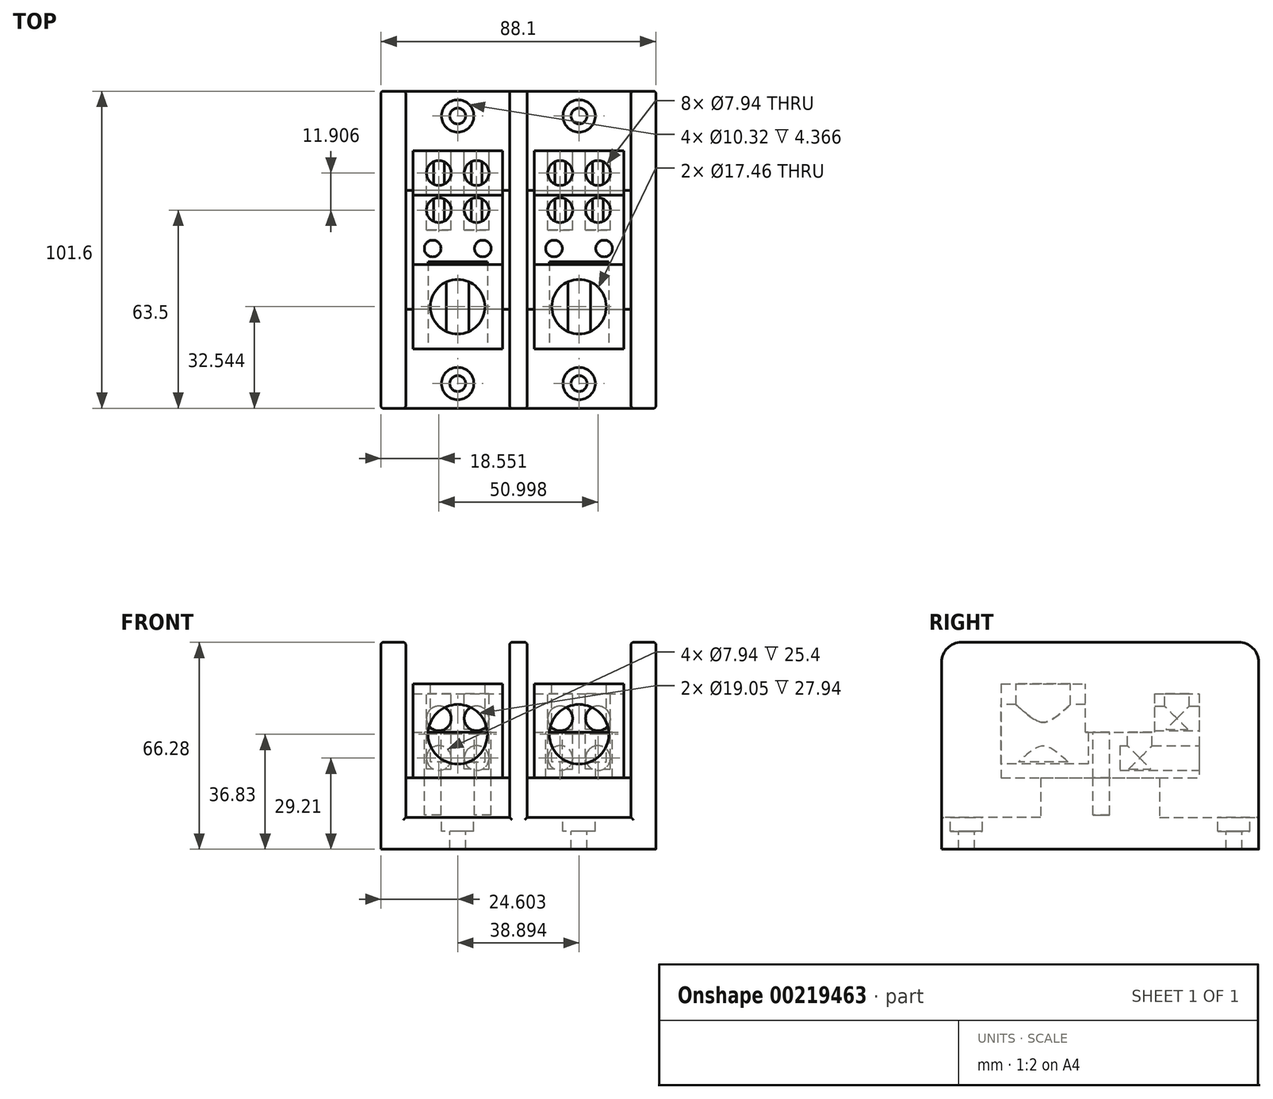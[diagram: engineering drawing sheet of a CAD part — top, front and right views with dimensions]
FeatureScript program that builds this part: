
annotation { "Feature Type Name" : "Feature", "Feature Type Description" : "" }
export const myFeature = defineFeature(function(context is Context, id is Id, definition is map)
    precondition{}
    {
        {
            var Q0;
            Q0=qCreatedBy(makeId("Top.planeOp"),FACE);
            var sketch = newSketch(context, id + "F0", { "sketchPlane" : qUnion([Q0])});
            skLineSegment(sketch, "E0.bottom", {"start": v(-44.05, -50.8) * mm, "end": v(44.05, -50.8) * mm});
            skLineSegment(sketch, "E0.top", {"start": v(-44.05, 50.8) * mm, "end": v(44.05, 50.8) * mm});
            skLineSegment(sketch, "E0.left", {"start": v(-44.05, -50.8) * mm, "end": v(-44.05, 50.8) * mm});
            skLineSegment(sketch, "E0.right", {"start": v(44.05, -50.8) * mm, "end": v(44.05, 50.8) * mm});
            skPoint(sketch, "E0.middle", {"position": v(0, 0) * mm});
            skSolve(sketch);
        }
        {
            var Q0;
            Q0=makeQuery(id+"F0.imprint","IMPRINT",FACE,{"disambiguationData":[TD([[makeQuery(id+"F0.imprint","IMPRINT",EDGE,{"derivedFrom":sQuery(id+"F0.wireOp",EDGE,"E0.bottom")}),1.0]])]});
            extrude(context, id + "F1", {"entities" : qUnion([Q0]), "depth" : 10.16 * mm});
        }
        {
            var Q0;
            Q0=makeQuery(id+"F1.opExtrude","CAP_FACE",FACE,{"disambiguationData":[OSD([sQuery(id+"F0.wireOp",EDGE,"E0.bottom"),sQuery(id+"F0.wireOp",EDGE,"E0.top"),sQuery(id+"F0.wireOp",EDGE,"E0.left"),sQuery(id+"F0.wireOp",EDGE,"E0.right")])],"isStart":false});
            var sketch = newSketch(context, id + "F2", { "sketchPlane" : qUnion([Q0])});
            skCircle(sketch, "E1", {"center": v(-19.45, 42.86) * mm, "radius": 2.54 * mm});
            skCircle(sketch, "E2", {"center": v(19.45, 42.86) * mm, "radius": 2.54 * mm});
            skCircle(sketch, "E3", {"center": v(-19.45, -42.86) * mm, "radius": 2.54 * mm});
            skCircle(sketch, "E4", {"center": v(19.45, -42.86) * mm, "radius": 2.54 * mm});
            skSolve(sketch);
        }
        {
            var Q0;
            Q0=qSketchRegion(id+"F2",true);
            extrude(context, id + "F3", {"entities" : qUnion([Q0]), "operationType" : NewBodyOperationType.REMOVE, "oppositeDirection" : true, "depth" : 10.16 * mm});
        }
        {
            var Q0;
            Q0=makeQuery(id+"F1.opExtrude","CAP_FACE",FACE,{"disambiguationData":[OSD([sQuery(id+"F0.wireOp",EDGE,"E0.bottom"),sQuery(id+"F0.wireOp",EDGE,"E0.top"),sQuery(id+"F0.wireOp",EDGE,"E0.left"),sQuery(id+"F0.wireOp",EDGE,"E0.right")])],"isStart":false});
            var sketch = newSketch(context, id + "F4", { "sketchPlane" : qUnion([Q0])});
            skCircle(sketch, "E5", {"center": v(-19.45, 42.86) * mm, "radius": 5.16 * mm});
            skCircle(sketch, "E6", {"center": v(19.45, 42.86) * mm, "radius": 5.16 * mm});
            skCircle(sketch, "E7", {"center": v(-19.45, -42.86) * mm, "radius": 5.16 * mm});
            skCircle(sketch, "E8", {"center": v(19.45, -42.86) * mm, "radius": 5.16 * mm});
            skSolve(sketch);
        }
        {
            var Q0;
            Q0=qSketchRegion(id+"F4",true);
            extrude(context, id + "F5", {"entities" : qUnion([Q0]), "operationType" : NewBodyOperationType.REMOVE, "oppositeDirection" : true, "depth" : 4.37 * mm});
        }
        {
            var Q0;
            Q0=makeQuery(id+"F1.opExtrude","CAP_FACE",FACE,{"disambiguationData":[OSD([sQuery(id+"F0.wireOp",EDGE,"E0.bottom"),sQuery(id+"F0.wireOp",EDGE,"E0.top"),sQuery(id+"F0.wireOp",EDGE,"E0.left"),sQuery(id+"F0.wireOp",EDGE,"E0.right")])],"isStart":false});
            var sketch = newSketch(context, id + "F6", { "sketchPlane" : qUnion([Q0])});
            skLineSegment(sketch, "E9.bottom", {"start": v(-2.78, -19.05) * mm, "end": v(-36.12, -19.05) * mm});
            skLineSegment(sketch, "E9.top", {"start": v(-2.78, 19.05) * mm, "end": v(-36.12, 19.05) * mm});
            skLineSegment(sketch, "E9.left", {"start": v(-2.78, -19.05) * mm, "end": v(-2.78, 19.05) * mm});
            skLineSegment(sketch, "E9.right", {"start": v(-36.12, -19.05) * mm, "end": v(-36.12, 19.05) * mm});
            skPoint(sketch, "E9.middle", {"position": v(-19.45, 0) * mm});
            skLineSegment(sketch, "E10.bottom", {"start": v(2.78, -19.05) * mm, "end": v(36.12, -19.05) * mm});
            skLineSegment(sketch, "E10.top", {"start": v(2.78, 19.05) * mm, "end": v(36.12, 19.05) * mm});
            skLineSegment(sketch, "E10.left", {"start": v(2.78, -19.05) * mm, "end": v(2.78, 19.05) * mm});
            skLineSegment(sketch, "E10.right", {"start": v(36.12, -19.05) * mm, "end": v(36.12, 19.05) * mm});
            skPoint(sketch, "E10.middle", {"position": v(19.45, 0) * mm});
            skSolve(sketch);
        }
        {
            var Q0;
            Q0=qSketchRegion(id+"F6",true);
            extrude(context, id + "F7", {"entities" : qUnion([Q0]), "operationType" : NewBodyOperationType.ADD, "depth" : 12.7 * mm});
        }
        {
            var Q0;
            Q0=makeQuery(id+"F1.opExtrude","CAP_FACE",FACE,{"disambiguationData":[OSD([sQuery(id+"F0.wireOp",EDGE,"E0.bottom"),sQuery(id+"F0.wireOp",EDGE,"E0.top"),sQuery(id+"F0.wireOp",EDGE,"E0.left"),sQuery(id+"F0.wireOp",EDGE,"E0.right")])],"isStart":false});
            var sketch = newSketch(context, id + "F8", { "sketchPlane" : qUnion([Q0])});
            skLineSegment(sketch, "E11.bottom", {"start": v(-36.12, 50.8) * mm, "end": v(-44.05, 50.8) * mm});
            skLineSegment(sketch, "E11.top", {"start": v(-36.12, -50.8) * mm, "end": v(-44.05, -50.8) * mm});
            skLineSegment(sketch, "E11.left", {"start": v(-36.12, 50.8) * mm, "end": v(-36.12, -50.8) * mm});
            skLineSegment(sketch, "E11.right", {"start": v(-44.05, 50.8) * mm, "end": v(-44.05, -50.8) * mm});
            skLineSegment(sketch, "E12.bottom", {"start": v(2.78, 50.8) * mm, "end": v(-2.78, 50.8) * mm});
            skLineSegment(sketch, "E12.top", {"start": v(2.78, -50.8) * mm, "end": v(-2.78, -50.8) * mm});
            skLineSegment(sketch, "E12.left", {"start": v(2.78, 50.8) * mm, "end": v(2.78, -50.8) * mm});
            skLineSegment(sketch, "E12.right", {"start": v(-2.78, 50.8) * mm, "end": v(-2.78, -50.8) * mm});
            skLineSegment(sketch, "E13.bottom", {"start": v(36.12, 50.8) * mm, "end": v(44.05, 50.8) * mm});
            skLineSegment(sketch, "E13.top", {"start": v(36.12, -50.8) * mm, "end": v(44.05, -50.8) * mm});
            skLineSegment(sketch, "E13.left", {"start": v(36.12, 50.8) * mm, "end": v(36.12, -50.8) * mm});
            skLineSegment(sketch, "E13.right", {"start": v(44.05, 50.8) * mm, "end": v(44.05, -50.8) * mm});
            skSolve(sketch);
        }
        {
            var Q0;
            Q0=qSketchRegion(id+"F8",true);
            extrude(context, id + "F9", {"entities" : qUnion([Q0]), "operationType" : NewBodyOperationType.ADD, "depth" : 56.12 * mm});
        }
        {
            var Q0;
            Q0=makeQuery(id+"F7.opExtrude","CAP_FACE",FACE,{"disambiguationData":[OSD([sQuery(id+"F6.wireOp",EDGE,"E9.bottom"),sQuery(id+"F6.wireOp",EDGE,"E9.top"),sQuery(id+"F6.wireOp",EDGE,"E9.left"),sQuery(id+"F6.wireOp",EDGE,"E9.right")])],"isStart":false});
            var sketch = newSketch(context, id + "F10", { "sketchPlane" : qUnion([Q0])});
            skLineSegment(sketch, "E14.bottom", {"start": v(-33.83, -31.75) * mm, "end": v(-5.06, -31.75) * mm});
            skLineSegment(sketch, "E14.top", {"start": v(-33.83, 31.75) * mm, "end": v(-5.06, 31.75) * mm});
            skLineSegment(sketch, "E14.left", {"start": v(-33.83, -31.75) * mm, "end": v(-33.83, 31.75) * mm});
            skLineSegment(sketch, "E14.right", {"start": v(-5.06, -31.75) * mm, "end": v(-5.06, 31.75) * mm});
            skPoint(sketch, "E14.middle", {"position": v(-19.45, 0) * mm});
            skSolve(sketch);
        }
        {
            var Q0;
            Q0=qSketchRegion(id+"F10",true);
            extrude(context, id + "F11", {"entities" : qUnion([Q0]), "depth" : 30.16 * mm});
        }
        {
            var Q0;
            Q0=makeQuery(id+"F11.opExtrude","CAP_FACE",FACE,{"disambiguationData":[OSD([sQuery(id+"F10.wireOp",EDGE,"E14.bottom"),sQuery(id+"F10.wireOp",EDGE,"E14.top"),sQuery(id+"F10.wireOp",EDGE,"E14.left"),sQuery(id+"F10.wireOp",EDGE,"E14.right")])],"isStart":false});
            var sketch = newSketch(context, id + "F12", { "sketchPlane" : qUnion([Q0])});
            skLineSegment(sketch, "E15.bottom", {"start": v(-33.83, -4.76) * mm, "end": v(-5.06, -4.76) * mm});
            skLineSegment(sketch, "E15.top", {"start": v(-33.83, 17.46) * mm, "end": v(-5.06, 17.46) * mm});
            skLineSegment(sketch, "E15.left", {"start": v(-33.83, -4.76) * mm, "end": v(-33.83, 17.46) * mm});
            skLineSegment(sketch, "E15.right", {"start": v(-5.06, -4.76) * mm, "end": v(-5.06, 17.46) * mm});
            skPoint(sketch, "E15.middle", {"position": v(-19.45, 6.35) * mm});
            skPoint(sketch, "E15.middle.positionSnap0", {"position": v(-19.45, -31.75) * mm});
            skPoint(sketch, "E15.centerSnap0", {"position": v(-19.45, -31.75) * mm});
            skSolve(sketch);
        }
        {
            var Q0;
            Q0=makeQuery(id+"F12.imprint","IMPRINT",FACE,{"disambiguationData":[TD([[makeQuery(id+"F12.imprint","IMPRINT",EDGE,{"derivedFrom":sQuery(id+"F12.wireOp",EDGE,"E15.bottom")}),1.0]])]});
            extrude(context, id + "F13", {"entities" : qUnion([Q0]), "operationType" : NewBodyOperationType.REMOVE, "oppositeDirection" : true, "depth" : 15.48 * mm});
        }
        {
            var Q0;
            {var subQ0=sQuery(id+"F10.wireOp",EDGE,"E14.top");var subQ1=sQuery(id+"F10.wireOp",EDGE,"E14.right");var subQ2=sQuery(id+"F10.wireOp",EDGE,"E14.left");Q0=makeQuery(id+"F13.boolean.opBoolean","SPLIT",FACE,{"disambiguationData":[TD([makeQuery(id+"F11.opExtrude","SWEPT_FACE",FACE,{"disambiguationData":[OSD([subQ0])]})])],"derivedFrom":makeQuery(id+"F11.opExtrude","CAP_FACE",FACE,{"disambiguationData":[OSD([sQuery(id+"F10.wireOp",EDGE,"E14.bottom"),subQ0,subQ2,subQ1])],"isStart":false})});}
            extrude(context, id + "F14", {"entities" : qUnion([Q0]), "operationType" : NewBodyOperationType.REMOVE, "oppositeDirection" : true, "depth" : 3.17 * mm});
        }
        {
            var Q0;
            {var subQ0=sQuery(id+"F10.wireOp",EDGE,"E14.bottom");var subQ1=sQuery(id+"F10.wireOp",EDGE,"E14.left");var subQ2=sQuery(id+"F10.wireOp",EDGE,"E14.right");Q0=makeQuery(id+"F13.boolean.opBoolean","SPLIT",FACE,{"disambiguationData":[TD([makeQuery(id+"F11.opExtrude","SWEPT_FACE",FACE,{"disambiguationData":[OSD([subQ0])]})])],"derivedFrom":makeQuery(id+"F11.opExtrude","CAP_FACE",FACE,{"disambiguationData":[OSD([subQ0,sQuery(id+"F10.wireOp",EDGE,"E14.top"),subQ1,subQ2])],"isStart":false})});}
            var sketch = newSketch(context, id + "F15", { "sketchPlane" : qUnion([Q0])});
            skCircle(sketch, "E16", {"center": v(-19.45, -18.26) * mm, "radius": 8.73 * mm});
            skPoint(sketch, "E16.centerSnap0", {"position": v(-5.06, -18.26) * mm});
            skPoint(sketch, "E16.centerSnap1", {"position": v(-19.45, -4.76) * mm});
            skSolve(sketch);
        }
        {
            var Q0;
            Q0=makeQuery(id+"F15.imprint","IMPRINT",FACE,{"disambiguationData":[TD([[makeQuery(id+"F15.imprint","IMPRINT",EDGE,{"derivedFrom":sQuery(id+"F15.wireOp",EDGE,"E16")}),1.0]])]});
            extrude(context, id + "F16", {"entities" : qUnion([Q0]), "operationType" : NewBodyOperationType.REMOVE, "oppositeDirection" : true, "depth" : 25 * mm});
        }
        {
            var Q0;
            Q0=makeQuery(id+"F11.opExtrude","SWEPT_FACE",FACE,{"disambiguationData":[OSD([sQuery(id+"F10.wireOp",EDGE,"E14.bottom")])]});
            var sketch = newSketch(context, id + "F17", { "sketchPlane" : qUnion([Q0])});
            skCircle(sketch, "E17", {"center": v(-19.45, 36.83) * mm, "radius": 9.53 * mm});
            skPoint(sketch, "E17.centerSnap0", {"position": v(-19.45, 53.02) * mm});
            skSolve(sketch);
        }
        {
            var Q0;
            Q0=makeQuery(id+"F17.imprint","IMPRINT",FACE,{"disambiguationData":[TD([[makeQuery(id+"F17.imprint","IMPRINT",EDGE,{"derivedFrom":sQuery(id+"F17.wireOp",EDGE,"E17")}),1.0]])]});
            extrude(context, id + "F18", {"entities" : qUnion([Q0]), "operationType" : NewBodyOperationType.REMOVE, "oppositeDirection" : true, "depth" : 27.94 * mm});
        }
        {
            var Q0;
            Q0=makeQuery(id+"F13.boolean.opBoolean","COPY",FACE,{"derivedFrom":makeQuery(id+"F13.opExtrude","CAP_FACE",FACE,{"disambiguationData":[OSD([sQuery(id+"F12.wireOp",EDGE,"E15.bottom"),sQuery(id+"F12.wireOp",EDGE,"E15.top"),sQuery(id+"F12.wireOp",EDGE,"E15.left"),sQuery(id+"F12.wireOp",EDGE,"E15.right")])],"isStart":false})});
            var sketch = newSketch(context, id + "F19", { "sketchPlane" : qUnion([Q0])});
            skCircle(sketch, "E18", {"center": v(-27.48, 0.4) * mm, "radius": 2.67 * mm});
            skCircle(sketch, "E19", {"center": v(-11.41, 0.4) * mm, "radius": 2.67 * mm});
            skCircle(sketch, "E20", {"center": v(-25.5, 12.7) * mm, "radius": 3.97 * mm});
            skCircle(sketch, "E21", {"center": v(-13.4, 12.7) * mm, "radius": 3.97 * mm});
            skSolve(sketch);
        }
        {
            var Q0;
            Q0=qSketchRegion(id+"F19",true);
            extrude(context, id + "F20", {"entities" : qUnion([Q0]), "operationType" : NewBodyOperationType.REMOVE, "oppositeDirection" : true, "depth" : 11.9 * mm});
        }
        {
            var Q0;
            Q0=makeQuery(id+"F20.boolean.opBoolean","COPY",FACE,{"derivedFrom":makeQuery(id+"F20.opExtrude","CAP_FACE",FACE,{"disambiguationData":[OSD([sQuery(id+"F19.wireOp",EDGE,"E18")])],"isStart":false})});
            var Q1;
            Q1=makeQuery(id+"F20.boolean.opBoolean","COPY",FACE,{"derivedFrom":makeQuery(id+"F20.opExtrude","CAP_FACE",FACE,{"disambiguationData":[OSD([sQuery(id+"F19.wireOp",EDGE,"E19")])],"isStart":false})});
            extrude(context, id + "F21", {"entities" : qUnion([Q0, Q1]), "operationType" : NewBodyOperationType.REMOVE, "oppositeDirection" : true, "depth" : 14.68 * mm});
        }
        {
            var Q0;
            Q0=makeQuery(id+"F14.boolean.opBoolean","COPY",FACE,{"derivedFrom":makeQuery(id+"F14.opExtrude","CAP_FACE",FACE,{"disambiguationData":[OSD([sQuery(id+"F10.wireOp",EDGE,"E14.bottom"),sQuery(id+"F10.wireOp",EDGE,"E14.top"),sQuery(id+"F10.wireOp",EDGE,"E14.left"),sQuery(id+"F10.wireOp",EDGE,"E14.right")])],"isStart":false})});
            var sketch = newSketch(context, id + "F22", { "sketchPlane" : qUnion([Q0])});
            skCircle(sketch, "E22", {"center": v(-25.5, 24.6) * mm, "radius": 3.97 * mm});
            skPoint(sketch, "E22.centerSnap0", {"position": v(-33.83, 24.6) * mm});
            skCircle(sketch, "E23", {"center": v(-13.4, 24.6) * mm, "radius": 3.97 * mm});
            skSolve(sketch);
        }
        {
            var Q0;
            Q0=qSketchRegion(id+"F22",true);
            extrude(context, id + "F23", {"entities" : qUnion([Q0]), "operationType" : NewBodyOperationType.REMOVE, "oppositeDirection" : true, "depth" : 11.5 * mm});
        }
        {
            var Q0;
            Q0=makeQuery(id+"F11.opExtrude","SWEPT_FACE",FACE,{"disambiguationData":[OSD([sQuery(id+"F10.wireOp",EDGE,"E14.top")])]});
            var sketch = newSketch(context, id + "F24", { "sketchPlane" : qUnion([Q0])});
            skCircle(sketch, "E24", {"center": v(13.4, 41.91) * mm, "radius": 3.97 * mm});
            skCircle(sketch, "E25", {"center": v(25.5, 41.91) * mm, "radius": 3.97 * mm});
            skCircle(sketch, "E26", {"center": v(13.4, 29.21) * mm, "radius": 3.97 * mm});
            skCircle(sketch, "E27", {"center": v(25.5, 29.21) * mm, "radius": 3.97 * mm});
            skSolve(sketch);
        }
        {
            var Q0;
            Q0=qSketchRegion(id+"F24",true);
            extrude(context, id + "F25", {"entities" : qUnion([Q0]), "operationType" : NewBodyOperationType.REMOVE, "oppositeDirection" : true, "depth" : 14.73 * mm});
        }
        {
            var Q0;
            Q0=makeQuery(id+"F25.boolean.opBoolean","COPY",FACE,{"derivedFrom":makeQuery(id+"F25.opExtrude","CAP_FACE",FACE,{"disambiguationData":[OSD([sQuery(id+"F24.wireOp",EDGE,"E26")])],"isStart":false})});
            var Q1;
            Q1=makeQuery(id+"F25.boolean.opBoolean","COPY",FACE,{"derivedFrom":makeQuery(id+"F25.opExtrude","CAP_FACE",FACE,{"disambiguationData":[OSD([sQuery(id+"F24.wireOp",EDGE,"E27")])],"isStart":false})});
            extrude(context, id + "F26", {"entities" : qUnion([Q0, Q1]), "operationType" : NewBodyOperationType.REMOVE, "oppositeDirection" : true, "depth" : 10.67 * mm});
        }
        {
            var Q0;
            Q0=makeQuery(id+"F11.opExtrude","SWEPT_BODY",BODY,{"disambiguationData":[OSD([sQuery(id+"F10.wireOp",EDGE,"E14.bottom"),sQuery(id+"F10.wireOp",EDGE,"E14.top"),sQuery(id+"F10.wireOp",EDGE,"E14.left"),sQuery(id+"F10.wireOp",EDGE,"E14.right")])]});
            transform(context, id + "F27", {"entities" : qUnion([Q0]), "transformType" : TransformType.TRANSLATION_3D, "dx" : 38.9 * mm, "dy" : 0 * mm, "dz" : 0 * mm, "makeCopy" : true});
        }
        {
            var Q0;
            Q0=makeQuery(id+"F9.opExtrude","CAP_EDGE",EDGE,{"disambiguationData":[OSD([sQuery(id+"F8.wireOp",EDGE,"E11.bottom")])],"isStart":false});
            var Q1;
            Q1=makeQuery(id+"F9.opExtrude","CAP_EDGE",EDGE,{"disambiguationData":[OSD([sQuery(id+"F8.wireOp",EDGE,"E12.bottom")])],"isStart":false});
            var Q2;
            Q2=makeQuery(id+"F9.opExtrude","CAP_EDGE",EDGE,{"disambiguationData":[OSD([sQuery(id+"F8.wireOp",EDGE,"E13.bottom")])],"isStart":false});
            var Q3;
            Q3=makeQuery(id+"F9.opExtrude","CAP_EDGE",EDGE,{"disambiguationData":[OSD([sQuery(id+"F8.wireOp",EDGE,"E11.top")])],"isStart":false});
            var Q4;
            Q4=makeQuery(id+"F9.opExtrude","CAP_EDGE",EDGE,{"disambiguationData":[OSD([sQuery(id+"F8.wireOp",EDGE,"E12.top")])],"isStart":false});
            var Q5;
            Q5=makeQuery(id+"F9.opExtrude","CAP_EDGE",EDGE,{"disambiguationData":[OSD([sQuery(id+"F8.wireOp",EDGE,"E13.top")])],"isStart":false});
            fillet(context, id + "F28", {"entities" : qUnion([Q0, Q1, Q2, Q3, Q4, Q5]), "radius" : 6.35 * mm, "tangentPropagation" : true});
        }
        {
            var Q0;
            Q0=makeQuery(id+"F9.boolean.opBoolean","MERGE",EDGE,{"derivedFrom":[makeQuery(id+"F1.opExtrude","SWEPT_EDGE",EDGE,{"disambiguationData":[OSD([sQuery(id+"F0.wireOp",EDGE,"E0.bottom"),sQuery(id+"F0.wireOp",EDGE,"E0.right")])]}),makeQuery(id+"F9.opExtrude","SWEPT_EDGE",EDGE,{"disambiguationData":[OSD([sQuery(id+"F8.wireOp",EDGE,"E13.top"),sQuery(id+"F8.wireOp",EDGE,"E13.right")])]})]});
            var Q1;
            Q1=makeQuery(id+"F9.opExtrude","SWEPT_EDGE",EDGE,{"disambiguationData":[OSD([sQuery(id+"F0.wireOp",EDGE,"E0.bottom"),sQuery(id+"F8.wireOp",EDGE,"E13.top"),sQuery(id+"F8.wireOp",EDGE,"E13.left")])]});
            var Q2;
            {var subQ0=sQuery(id+"F0.wireOp",EDGE,"E0.bottom");Q2=makeQuery(id+"F9.boolean.opBoolean","SPLIT",EDGE,{"disambiguationData":[TD([makeQuery(id+"F9.opExtrude","SWEPT_FACE",FACE,{"disambiguationData":[OSD([sQuery(id+"F8.wireOp",EDGE,"E12.left")])]})])],"derivedFrom":makeQuery(id+"F1.opExtrude","CAP_EDGE",EDGE,{"disambiguationData":[OSD([subQ0])],"isStart":false})});}
            var Q3;
            Q3=makeQuery(id+"F9.opExtrude","SWEPT_EDGE",EDGE,{"disambiguationData":[OSD([sQuery(id+"F0.wireOp",EDGE,"E0.bottom"),sQuery(id+"F8.wireOp",EDGE,"E12.top"),sQuery(id+"F8.wireOp",EDGE,"E12.left")])]});
            var Q4;
            Q4=makeQuery(id+"F9.opExtrude","SWEPT_EDGE",EDGE,{"disambiguationData":[OSD([sQuery(id+"F0.wireOp",EDGE,"E0.bottom"),sQuery(id+"F8.wireOp",EDGE,"E12.top"),sQuery(id+"F8.wireOp",EDGE,"E12.right")])]});
            var Q5;
            {var subQ0=sQuery(id+"F0.wireOp",EDGE,"E0.bottom");Q5=makeQuery(id+"F9.boolean.opBoolean","SPLIT",EDGE,{"disambiguationData":[TD([makeQuery(id+"F9.opExtrude","SWEPT_FACE",FACE,{"disambiguationData":[OSD([sQuery(id+"F8.wireOp",EDGE,"E11.left")])]})])],"derivedFrom":makeQuery(id+"F1.opExtrude","CAP_EDGE",EDGE,{"disambiguationData":[OSD([subQ0])],"isStart":false})});}
            var Q6;
            Q6=makeQuery(id+"F9.opExtrude","SWEPT_EDGE",EDGE,{"disambiguationData":[OSD([sQuery(id+"F0.wireOp",EDGE,"E0.bottom"),sQuery(id+"F8.wireOp",EDGE,"E11.top"),sQuery(id+"F8.wireOp",EDGE,"E11.left")])]});
            var Q7;
            Q7=makeQuery(id+"F9.boolean.opBoolean","MERGE",EDGE,{"derivedFrom":[makeQuery(id+"F1.opExtrude","SWEPT_EDGE",EDGE,{"disambiguationData":[OSD([sQuery(id+"F0.wireOp",EDGE,"E0.bottom"),sQuery(id+"F0.wireOp",EDGE,"E0.left")])]}),makeQuery(id+"F9.opExtrude","SWEPT_EDGE",EDGE,{"disambiguationData":[OSD([sQuery(id+"F8.wireOp",EDGE,"E11.top"),sQuery(id+"F8.wireOp",EDGE,"E11.right")])]})]});
            var Q8;
            {var subQ0=sQuery(id+"F0.wireOp",EDGE,"E0.top");Q8=makeQuery(id+"F9.boolean.opBoolean","SPLIT",EDGE,{"disambiguationData":[TD([makeQuery(id+"F9.opExtrude","SWEPT_FACE",FACE,{"disambiguationData":[OSD([sQuery(id+"F8.wireOp",EDGE,"E11.left")])]})])],"derivedFrom":makeQuery(id+"F1.opExtrude","CAP_EDGE",EDGE,{"disambiguationData":[OSD([subQ0])],"isStart":false})});}
            var Q9;
            {var subQ0=sQuery(id+"F0.wireOp",EDGE,"E0.top");Q9=makeQuery(id+"F9.boolean.opBoolean","SPLIT",EDGE,{"disambiguationData":[TD([makeQuery(id+"F9.opExtrude","SWEPT_FACE",FACE,{"disambiguationData":[OSD([sQuery(id+"F8.wireOp",EDGE,"E12.left")])]})])],"derivedFrom":makeQuery(id+"F1.opExtrude","CAP_EDGE",EDGE,{"disambiguationData":[OSD([subQ0])],"isStart":false})});}
            fillet(context, id + "F29", {"entities" : qUnion([Q0, Q1, Q2, Q3, Q4, Q5, Q6, Q7, Q8, Q9]), "radius" : 0.76 * mm, "tangentPropagation" : true});
        }
    });
